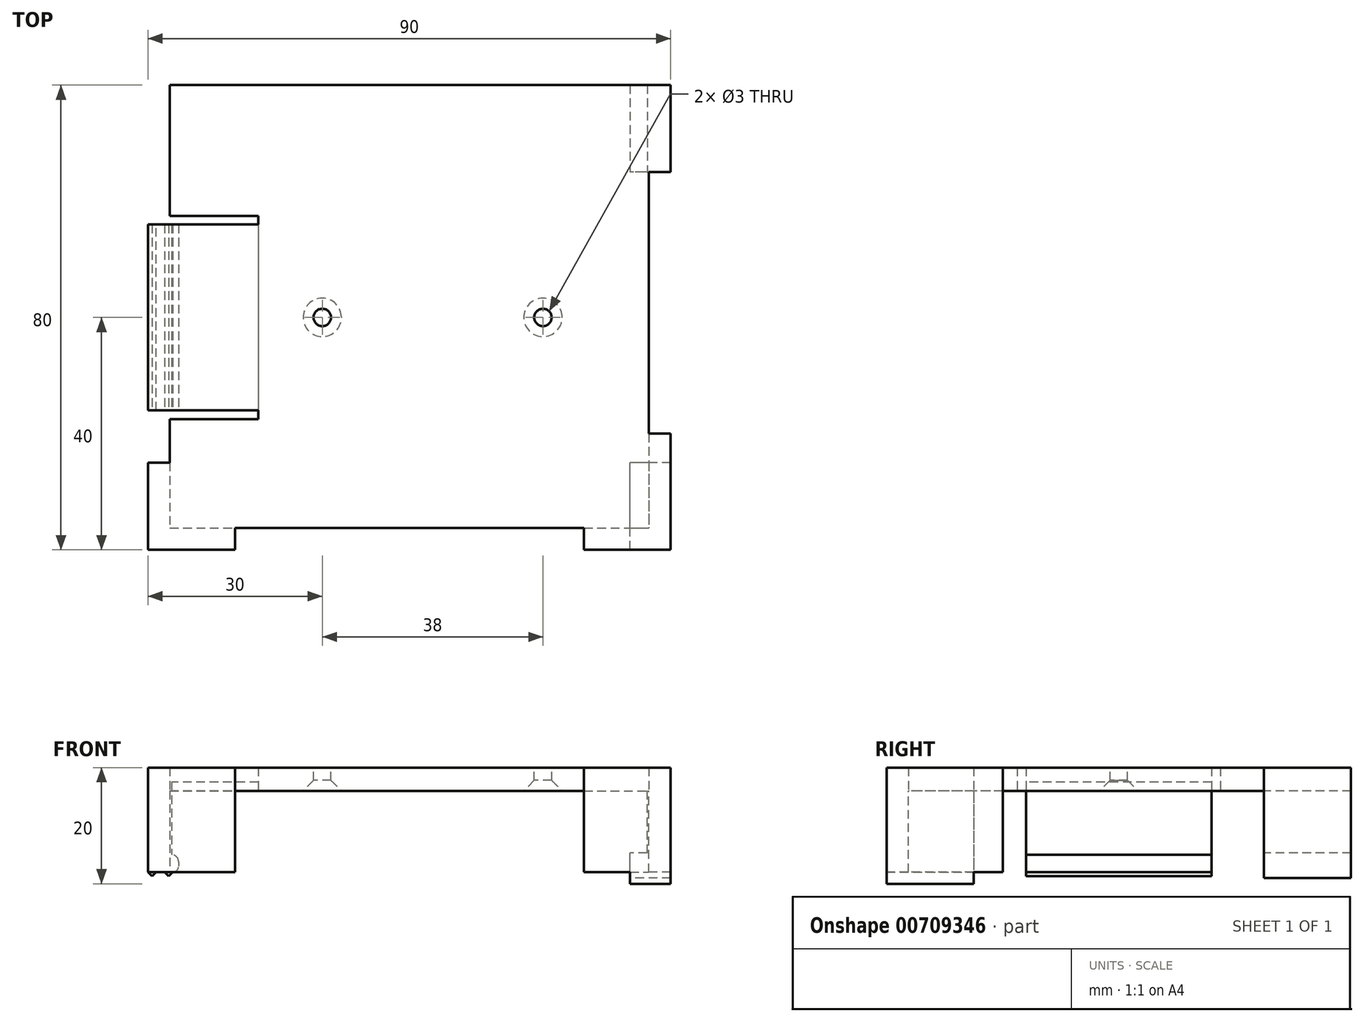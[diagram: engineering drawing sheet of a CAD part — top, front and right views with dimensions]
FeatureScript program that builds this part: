
annotation { "Feature Type Name" : "Feature", "Feature Type Description" : "" }
export const myFeature = defineFeature(function(context is Context, id is Id, definition is map)
    precondition{}
    {
        {
            var Q0;
            Q0=qCreatedBy(makeId("Top.planeOp"),FACE);
            var sketch = newSketch(context, id + "F0", { "sketchPlane" : qUnion([Q0])});
            skLineSegment(sketch, "E0.bottom", {"start": v(-45, -40) * mm, "end": v(45, -40) * mm});
            skLineSegment(sketch, "E0.top", {"start": v(-45, 40) * mm, "end": v(45, 40) * mm});
            skLineSegment(sketch, "E0.left", {"start": v(-45, -40) * mm, "end": v(-45, 40) * mm});
            skLineSegment(sketch, "E0.right", {"start": v(45, -40) * mm, "end": v(45, 40) * mm});
            skPoint(sketch, "E0.middle", {"position": v(0, 0) * mm});
            skSolve(sketch);
        }
        {
            var Q0;
            Q0 = qSketchRegion(id + "F0", true);
            extrude(context, id + "F1", {"entities" : qUnion([Q0]), "depth" : 4 * mm, "offsetDistance" : 25 * mm});
        }
        {
            var Q0;
            Q0=makeQuery(id+"F1.opExtrude","CAP_FACE",FACE,{"disambiguationData":[OSD([sQuery(id+"F0.wireOp",EDGE,"E0.bottom"),sQuery(id+"F0.wireOp",EDGE,"E0.top"),sQuery(id+"F0.wireOp",EDGE,"E0.left"),sQuery(id+"F0.wireOp",EDGE,"E0.right")])],"isStart":false});
            var sketch = newSketch(context, id + "F2", { "sketchPlane" : qUnion([Q0])});
            skCircle(sketch, "E1", {"center": v(23, 0) * mm, "radius": 1.5 * mm});
            skCircle(sketch, "E2", {"center": v(-15, 0) * mm, "radius": 1.5 * mm});
            skSolve(sketch);
        }
        {
            var Q0;
            Q0 = qSketchRegion(id + "F2", true);
            extrude(context, id + "F3", {"entities" : qUnion([Q0]), "operationType" : NewBodyOperationType.REMOVE, "endBound" : BoundingType.THROUGH_ALL, "oppositeDirection" : true, "depth" : 25 * mm, "offsetDistance" : 25 * mm});
        }
        {
            var Q0;
            Q0=makeQuery(id+"F1.opExtrude","CAP_FACE",FACE,{"disambiguationData":[OSD([sQuery(id+"F0.wireOp",EDGE,"E0.bottom"),sQuery(id+"F0.wireOp",EDGE,"E0.top"),sQuery(id+"F0.wireOp",EDGE,"E0.left"),sQuery(id+"F0.wireOp",EDGE,"E0.right")])],"isStart":true});
            var sketch = newSketch(context, id + "F4", { "sketchPlane" : qUnion([Q0])});
            skLineSegment(sketch, "E3.top", {"start": v(-41.25, 36.25) * mm, "end": v(-30, 36.25) * mm});
            skLineSegment(sketch, "E3.left", {"start": v(-41.25, -36.25) * mm, "end": v(-41.25, 36.25) * mm});
            skLineSegment(sketch, "E3.right", {"start": v(41.25, -36.25) * mm, "end": v(41.25, 36.25) * mm});
            skPoint(sketch, "E3.middle", {"position": v(0, 0) * mm});
            skLineSegment(sketch, "E4.top", {"start": v(-41.25, -40) * mm, "end": v(41.25, -40) * mm});
            skLineSegment(sketch, "E5", {"start": v(41.25, -40) * mm, "end": v(41.25, -36.25) * mm});
            skLineSegment(sketch, "E6", {"start": v(-41.25, -40) * mm, "end": v(-41.25, -36.25) * mm});
            skLineSegment(sketch, "E7.left", {"start": v(30, 36.25) * mm, "end": v(30, 40) * mm});
            skLineSegment(sketch, "E7.right", {"start": v(-30, 36.25) * mm, "end": v(-30, 40) * mm});
            skLineSegment(sketch, "E8.trimOffspring", {"start": v(30, 36.25) * mm, "end": v(41.25, 36.25) * mm});
            skSolve(sketch);
        }
        {
            var Q0;
            Q0=makeQuery(id+"F4.imprint","IMPRINT",FACE,{"disambiguationData":[TD([[makeQuery(id+"F4.imprint","IMPRINT",EDGE,{"derivedFrom":sQuery(id+"F4.wireOp",EDGE,"E3.top")}),1.0]])]});
            var Q1;
            Q1=makeQuery(id+"F4.imprint","IMPRINT",FACE,{"disambiguationData":[TD([[makeQuery(id+"F4.imprint","IMPRINT",EDGE,{"derivedFrom":sQuery(id+"F4.wireOp",EDGE,"E3.right")}),-1.0]])]});
            extrude(context, id + "F5", {"entities" : qUnion([Q0, Q1]), "operationType" : NewBodyOperationType.ADD, "depth" : 14 * mm, "offsetDistance" : 25 * mm});
        }
        {
            var Q0;
            Q0=makeQuery(id+"F5.opExtrude","CAP_FACE",FACE,{"disambiguationData":[OSD([sQuery(id+"F0.wireOp",EDGE,"E0.bottom"),sQuery(id+"F0.wireOp",EDGE,"E0.top"),sQuery(id+"F0.wireOp",EDGE,"E0.left"),sQuery(id+"F0.wireOp",EDGE,"E0.right"),sQuery(id+"F4.wireOp",EDGE,"E3.top"),sQuery(id+"F4.wireOp",EDGE,"E3.left"),sQuery(id+"F4.wireOp",EDGE,"E3.right"),sQuery(id+"F4.wireOp",EDGE,"E5"),sQuery(id+"F4.wireOp",EDGE,"E6")])],"isStart":false});
            var sketch = newSketch(context, id + "F6", { "sketchPlane" : qUnion([Q0])});
            skLineSegment(sketch, "E9.top", {"start": v(45, 25) * mm, "end": v(38, 25) * mm});
            skLineSegment(sketch, "E9.right", {"start": v(38, 40) * mm, "end": v(38, 25) * mm});
            skLineSegment(sketch, "E10", {"start": v(45, 40) * mm, "end": v(38, 40) * mm});
            skLineSegment(sketch, "E11", {"start": v(45, 40) * mm, "end": v(45, 25) * mm});
            skSolve(sketch);
        }
        {
            var Q0;
            Q0 = qSketchRegion(id + "F6", true);
            extrude(context, id + "F7", {"entities" : qUnion([Q0]), "operationType" : NewBodyOperationType.ADD, "depth" : 2 * mm, "offsetDistance" : 25 * mm});
        }
        {
            var Q0;
            {var subQ0=sQuery(id+"F4.wireOp",EDGE,"E5");var subQ1=sQuery(id+"F4.wireOp",EDGE,"E3.right");var subQ2=sQuery(id+"F0.wireOp",EDGE,"E0.right");var subQ3=sQuery(id+"F0.wireOp",EDGE,"E0.top");var subQ4=sQuery(id+"F0.wireOp",EDGE,"E0.left");var subQ6=sQuery(id+"F4.wireOp",EDGE,"E6");Q0=makeQuery(id+"F7.boolean.opBoolean","SPLIT",FACE,{"disambiguationData":[TD([makeQuery(id+"F1.opExtrude","SWEPT_FACE",FACE,{"disambiguationData":[OSD([subQ2])]})])],"derivedFrom":makeQuery(id+"F5.opExtrude","CAP_FACE",FACE,{"disambiguationData":[OSD([sQuery(id+"F0.wireOp",EDGE,"E0.bottom"),subQ3,subQ4,subQ2,sQuery(id+"F4.wireOp",EDGE,"E3.top"),sQuery(id+"F4.wireOp",EDGE,"E3.left"),subQ1,subQ0,subQ6])],"isStart":false})});}
            var sketch = newSketch(context, id + "F8", { "sketchPlane" : qUnion([Q0])});
            skLineSegment(sketch, "E12.bottom", {"start": v(45, -40) * mm, "end": v(41.25, -40) * mm});
            skLineSegment(sketch, "E12.top", {"start": v(45, 20) * mm, "end": v(41.25, 20) * mm});
            skLineSegment(sketch, "E12.left", {"start": v(45, -40) * mm, "end": v(45, 20) * mm});
            skLineSegment(sketch, "E12.right", {"start": v(41.25, -40) * mm, "end": v(41.25, 20) * mm});
            skSolve(sketch);
        }
        {
            var Q0;
            Q0 = qSketchRegion(id + "F8", true);
            extrude(context, id + "F9", {"entities" : qUnion([Q0]), "operationType" : NewBodyOperationType.REMOVE, "oppositeDirection" : true, "depth" : 2 * mm, "offsetDistance" : 25 * mm});
        }
        {
            var Q0;
            Q0=makeQuery(id+"F9.boolean.opBoolean","COPY",FACE,{"derivedFrom":makeQuery(id+"F9.opExtrude","CAP_FACE",FACE,{"disambiguationData":[OSD([sQuery(id+"F8.wireOp",EDGE,"E12.bottom"),sQuery(id+"F8.wireOp",EDGE,"E12.top"),sQuery(id+"F8.wireOp",EDGE,"E12.left"),sQuery(id+"F8.wireOp",EDGE,"E12.right")])],"isStart":false})});
            var sketch = newSketch(context, id + "F10", { "sketchPlane" : qUnion([Q0])});
            skLineSegment(sketch, "E13.bottom", {"start": v(45, -40) * mm, "end": v(41.25, -40) * mm});
            skLineSegment(sketch, "E13.top", {"start": v(45, -25) * mm, "end": v(41.25, -25) * mm});
            skLineSegment(sketch, "E13.left", {"start": v(45, -40) * mm, "end": v(45, -25) * mm});
            skLineSegment(sketch, "E14.bottom", {"start": v(41.25, -40) * mm, "end": v(38, -40) * mm});
            skLineSegment(sketch, "E14.top", {"start": v(41.25, -25) * mm, "end": v(38, -25) * mm});
            skLineSegment(sketch, "E14.left", {"start": v(41.25, -40) * mm, "end": v(41.25, -25) * mm});
            skLineSegment(sketch, "E14.right", {"start": v(38, -40) * mm, "end": v(38, -25) * mm});
            skSolve(sketch);
        }
        {
            var Q0;
            Q0 = qSketchRegion(id + "F10", true);
            extrude(context, id + "F11", {"entities" : qUnion([Q0]), "operationType" : NewBodyOperationType.ADD, "depth" : 3 * mm, "offsetDistance" : 25 * mm});
        }
        {
            var Q0;
            Q0=makeQuery(id+"F9.boolean.opBoolean","COPY",FACE,{"derivedFrom":makeQuery(id+"F9.opExtrude","CAP_FACE",FACE,{"disambiguationData":[OSD([sQuery(id+"F8.wireOp",EDGE,"E12.bottom"),sQuery(id+"F8.wireOp",EDGE,"E12.top"),sQuery(id+"F8.wireOp",EDGE,"E12.left"),sQuery(id+"F8.wireOp",EDGE,"E12.right")])],"isStart":false})});
            var sketch = newSketch(context, id + "F12", { "sketchPlane" : qUnion([Q0])});
            skLineSegment(sketch, "E15.bottom", {"start": v(45, -25) * mm, "end": v(41.25, -25) * mm});
            skLineSegment(sketch, "E15.top", {"start": v(45, 20) * mm, "end": v(41.25, 20) * mm});
            skLineSegment(sketch, "E15.left", {"start": v(45, -25) * mm, "end": v(45, 20) * mm});
            skLineSegment(sketch, "E15.right", {"start": v(41.25, -25) * mm, "end": v(41.25, 20) * mm});
            skSolve(sketch);
        }
        {
            var Q0;
            Q0 = qSketchRegion(id + "F12", true);
            extrude(context, id + "F13", {"entities" : qUnion([Q0]), "operationType" : NewBodyOperationType.REMOVE, "endBound" : BoundingType.THROUGH_ALL, "oppositeDirection" : true, "depth" : 25 * mm, "offsetDistance" : 25 * mm});
        }
        {
            var Q0;
            {var subQ0=sQuery(id+"F0.wireOp",EDGE,"E0.right");var subQ1=sQuery(id+"F0.wireOp",EDGE,"E0.top");var subQ3=sQuery(id+"F4.wireOp",EDGE,"E5");var subQ5=sQuery(id+"F0.wireOp",EDGE,"E0.left");var subQ6=sQuery(id+"F4.wireOp",EDGE,"E6");var subQ9=sQuery(id+"F0.wireOp",EDGE,"E0.bottom");var subQ10=sQuery(id+"F4.wireOp",EDGE,"E3.top");var subQ11=sQuery(id+"F4.wireOp",EDGE,"E3.left");Q0=makeQuery(id+"F7.boolean.opBoolean","SPLIT",FACE,{"disambiguationData":[TD([makeQuery(id+"F1.opExtrude","SWEPT_FACE",FACE,{"disambiguationData":[OSD([subQ9])]})])],"derivedFrom":makeQuery(id+"F5.opExtrude","CAP_FACE",FACE,{"disambiguationData":[OSD([subQ9,subQ1,subQ5,subQ0,subQ10,subQ11,sQuery(id+"F4.wireOp",EDGE,"E3.right"),subQ3,subQ6])],"isStart":false})});}
            var sketch = newSketch(context, id + "F14", { "sketchPlane" : qUnion([Q0])});
            skLineSegment(sketch, "E16.bottom", {"start": v(-45, 16) * mm, "end": v(-26, 16) * mm});
            skLineSegment(sketch, "E16.top", {"start": v(-45, 17.5) * mm, "end": v(-26, 17.5) * mm});
            skLineSegment(sketch, "E16.left", {"start": v(-45, 16) * mm, "end": v(-45, 17.5) * mm});
            skLineSegment(sketch, "E16.right", {"start": v(-26, 16) * mm, "end": v(-26, 17.5) * mm});
            skLineSegment(sketch, "E17.bottom", {"start": v(-45, -16) * mm, "end": v(-26, -16) * mm});
            skLineSegment(sketch, "E17.top", {"start": v(-45, -17.5) * mm, "end": v(-26, -17.5) * mm});
            skLineSegment(sketch, "E17.left", {"start": v(-45, -16) * mm, "end": v(-45, -17.5) * mm});
            skLineSegment(sketch, "E17.right", {"start": v(-26, -16) * mm, "end": v(-26, -17.5) * mm});
            skSolve(sketch);
        }
        {
            var Q0;
            Q0 = qSketchRegion(id + "F14", true);
            extrude(context, id + "F15", {"entities" : qUnion([Q0]), "operationType" : NewBodyOperationType.REMOVE, "oppositeDirection" : true, "depth" : 25 * mm, "offsetDistance" : 25 * mm});
        }
        {
            var Q0;
            {var subQ0=sQuery(id+"F4.wireOp",EDGE,"E6");var subQ1=sQuery(id+"F4.wireOp",EDGE,"E3.left");var subQ3=sQuery(id+"F0.wireOp",EDGE,"E0.left");var subQ6=sQuery(id+"F0.wireOp",EDGE,"E0.top");var subQ7=makeQuery(id+"F1.opExtrude","SWEPT_FACE",FACE,{"disambiguationData":[OSD([subQ6])]});var subQ11=sQuery(id+"F0.wireOp",EDGE,"E0.right");var subQ12=sQuery(id+"F4.wireOp",EDGE,"E5");var subQ16=sQuery(id+"F0.wireOp",EDGE,"E0.bottom");var subQ17=sQuery(id+"F4.wireOp",EDGE,"E3.top");Q0=makeQuery(id+"F15.boolean.opBoolean","SPLIT",FACE,{"disambiguationData":[TD([subQ7])],"derivedFrom":makeQuery(id+"F7.boolean.opBoolean","SPLIT",FACE,{"disambiguationData":[TD([makeQuery(id+"F1.opExtrude","SWEPT_FACE",FACE,{"disambiguationData":[OSD([subQ16])]})])],"derivedFrom":makeQuery(id+"F5.opExtrude","CAP_FACE",FACE,{"disambiguationData":[OSD([subQ16,subQ6,subQ3,subQ11,subQ17,subQ1,sQuery(id+"F4.wireOp",EDGE,"E3.right"),subQ12,subQ0])],"isStart":false})})});}
            var sketch = newSketch(context, id + "F16", { "sketchPlane" : qUnion([Q0])});
            skLineSegment(sketch, "E18.bottom", {"start": v(-41.25, -40) * mm, "end": v(-45, -40) * mm});
            skLineSegment(sketch, "E18.top", {"start": v(-41.25, -17.5) * mm, "end": v(-45, -17.5) * mm});
            skLineSegment(sketch, "E18.left", {"start": v(-41.25, -40) * mm, "end": v(-41.25, -17.5) * mm});
            skLineSegment(sketch, "E18.right", {"start": v(-45, -40) * mm, "end": v(-45, -17.5) * mm});
            skSolve(sketch);
        }
        {
            var Q0;
            Q0 = qSketchRegion(id + "F16", true);
            var Q1;
            Q1=makeQuery(id+"F1.opExtrude","CAP_FACE",FACE,{"disambiguationData":[OSD([sQuery(id+"F0.wireOp",EDGE,"E0.bottom"),sQuery(id+"F0.wireOp",EDGE,"E0.top"),sQuery(id+"F0.wireOp",EDGE,"E0.left"),sQuery(id+"F0.wireOp",EDGE,"E0.right")])],"isStart":true});
            extrude(context, id + "F17", {"entities" : qUnion([Q0]), "operationType" : NewBodyOperationType.REMOVE, "oppositeDirection" : true, "depth" : 25 * mm, "endBoundEntityFace" : qUnion([Q1]), "offsetDistance" : 25 * mm});
        }
        {
            var Q0;
            {var subQ4=sQuery(id+"F4.wireOp",EDGE,"E6");var subQ5=sQuery(id+"F4.wireOp",EDGE,"E3.left");Q0=makeQuery(id+"F15.boolean.opBoolean","SPLIT",FACE,{"disambiguationData":[TD([makeQuery(id+"F15.opExtrude","SWEPT_FACE",FACE,{"disambiguationData":[OSD([sQuery(id+"F14.wireOp",EDGE,"E16.bottom")])]})])],"derivedFrom":makeQuery(id+"F5.opExtrude","SWEPT_FACE",FACE,{"disambiguationData":[OSD([subQ5,subQ4])]})});}
            var sketch = newSketch(context, id + "F18", { "sketchPlane" : qUnion([Q0])});
            skLineSegment(sketch, "E19.bottom", {"start": v(16, -14) * mm, "end": v(-16, -14) * mm});
            skLineSegment(sketch, "E19.top", {"start": v(16, -12) * mm, "end": v(-16, -12) * mm});
            skLineSegment(sketch, "E19.left", {"start": v(16, -14) * mm, "end": v(16, -12) * mm});
            skLineSegment(sketch, "E19.right", {"start": v(-16, -14) * mm, "end": v(-16, -12) * mm});
            skSolve(sketch);
        }
        {
            var Q0;
            Q0=makeQuery(id+"F18.imprint","IMPRINT",FACE,{"disambiguationData":[TD([[makeQuery(id+"F18.imprint","IMPRINT",EDGE,{"derivedFrom":sQuery(id+"F18.wireOp",EDGE,"E19.bottom")}),-1.0]])]});
            extrude(context, id + "F19", {"entities" : qUnion([Q0]), "operationType" : NewBodyOperationType.ADD, "depth" : 1.5 * mm, "offsetDistance" : 25 * mm});
        }
        {
            var Q0;
            Q0=makeQuery(id+"F19.opExtrude","CAP_EDGE",EDGE,{"disambiguationData":[OSD([sQuery(id+"F18.wireOp",EDGE,"E19.bottom")])],"isStart":false});
            fillet(context, id + "F20", {"entities" : qUnion([Q0]), "radius" : 1 * mm, "tangentPropagation" : true, "allowEdgeOverflow" : false});
        }
        {
            var Q0;
            {var subQ0=sQuery(id+"F4.wireOp",EDGE,"E6");var subQ1=sQuery(id+"F4.wireOp",EDGE,"E3.left");var subQ3=sQuery(id+"F0.wireOp",EDGE,"E0.left");var subQ6=sQuery(id+"F0.wireOp",EDGE,"E0.right");var subQ7=sQuery(id+"F0.wireOp",EDGE,"E0.top");var subQ9=sQuery(id+"F4.wireOp",EDGE,"E5");var subQ13=sQuery(id+"F0.wireOp",EDGE,"E0.bottom");var subQ14=sQuery(id+"F4.wireOp",EDGE,"E3.top");Q0=makeQuery(id+"F19.boolean.opBoolean","MERGE",FACE,{"derivedFrom":[makeQuery(id+"F15.boolean.opBoolean","SPLIT",FACE,{"disambiguationData":[TD([makeQuery(id+"F15.opExtrude","SWEPT_FACE",FACE,{"disambiguationData":[OSD([sQuery(id+"F14.wireOp",EDGE,"E16.bottom")])]})])],"derivedFrom":makeQuery(id+"F7.boolean.opBoolean","SPLIT",FACE,{"disambiguationData":[TD([makeQuery(id+"F1.opExtrude","SWEPT_FACE",FACE,{"disambiguationData":[OSD([subQ13])]})])],"derivedFrom":makeQuery(id+"F5.opExtrude","CAP_FACE",FACE,{"disambiguationData":[OSD([subQ13,subQ7,subQ3,subQ6,subQ14,subQ1,sQuery(id+"F4.wireOp",EDGE,"E3.right"),subQ9,subQ0])],"isStart":false})})}),makeQuery(id+"F19.opExtrude","SWEPT_FACE",FACE,{"disambiguationData":[OSD([sQuery(id+"F18.wireOp",EDGE,"E19.bottom")])]})]});}
            var sketch = newSketch(context, id + "F21", { "sketchPlane" : qUnion([Q0])});
            skLineSegment(sketch, "E20.bottom", {"start": v(-40.75, -16) * mm, "end": v(-42.17, -16) * mm});
            skLineSegment(sketch, "E20.top", {"start": v(-40.75, 16) * mm, "end": v(-42.17, 16) * mm});
            skLineSegment(sketch, "E20.left", {"start": v(-40.75, -16) * mm, "end": v(-40.75, 16) * mm});
            skLineSegment(sketch, "E20.right", {"start": v(-42.17, -16) * mm, "end": v(-42.17, 16) * mm});
            skLineSegment(sketch, "E21.bottom", {"start": v(-45, 16) * mm, "end": v(-43.58, 16) * mm});
            skLineSegment(sketch, "E21.top", {"start": v(-45, -16) * mm, "end": v(-43.58, -16) * mm});
            skLineSegment(sketch, "E21.left", {"start": v(-45, 16) * mm, "end": v(-45, -16) * mm});
            skLineSegment(sketch, "E21.right", {"start": v(-43.58, 16) * mm, "end": v(-43.58, -16) * mm});
            skSolve(sketch);
        }
        {
            var Q0;
            Q0 = qSketchRegion(id + "F21", true);
            extrude(context, id + "F22", {"entities" : qUnion([Q0]), "operationType" : NewBodyOperationType.ADD, "depth" : (1.42 / 2) * mm, "offsetDistance" : 25 * mm});
        }
        {
            var Q0;
            Q0=makeQuery(id+"F22.opExtrude","CAP_EDGE",EDGE,{"disambiguationData":[OSD([sQuery(id+"F21.wireOp",EDGE,"E20.left")])],"isStart":false});
            var Q1;
            Q1=makeQuery(id+"F22.opExtrude","CAP_EDGE",EDGE,{"disambiguationData":[OSD([sQuery(id+"F21.wireOp",EDGE,"E20.right")])],"isStart":false});
            var Q2;
            Q2=makeQuery(id+"F22.opExtrude","CAP_EDGE",EDGE,{"disambiguationData":[OSD([sQuery(id+"F21.wireOp",EDGE,"o1l8Pqun-URdb-0TMV-Lpvj-JEDRhUXDJmeT.right")])],"isStart":false});
            var Q3;
            Q3=makeQuery(id+"F22.opExtrude","CAP_EDGE",EDGE,{"disambiguationData":[OSD([sQuery(id+"F21.wireOp",EDGE,"o1l8Pqun-URdb-0TMV-Lpvj-JEDRhUXDJmeT.left")])],"isStart":false});
            var Q4;
            Q4=makeQuery(id+"F22.opExtrude","CAP_EDGE",EDGE,{"disambiguationData":[OSD([sQuery(id+"F21.wireOp",EDGE,"E21.right")])],"isStart":false});
            var Q5;
            Q5=makeQuery(id+"F22.opExtrude","CAP_EDGE",EDGE,{"disambiguationData":[OSD([sQuery(id+"F21.wireOp",EDGE,"E21.left")])],"isStart":false});
            chamfer(context, id + "F23", {"entities" : qUnion([Q0, Q1, Q2, Q3, Q4, Q5]), "width" : (1.42 / 2) * mm, "tangentPropagation" : true});
        }
        {
            var Q0;
            Q0=makeQuery(id+"F3.boolean.opBoolean","INTERSECT",EDGE,{"derivedFrom":[makeQuery(id+"F1.opExtrude","CAP_FACE",FACE,{"disambiguationData":[OSD([sQuery(id+"F0.wireOp",EDGE,"E0.bottom"),sQuery(id+"F0.wireOp",EDGE,"E0.top"),sQuery(id+"F0.wireOp",EDGE,"E0.left"),sQuery(id+"F0.wireOp",EDGE,"E0.right")])],"isStart":true}),makeQuery(id+"F3.opExtrude","SWEPT_FACE",FACE,{"disambiguationData":[OSD([sQuery(id+"F2.wireOp",EDGE,"E2")])]})]});
            var Q1;
            Q1=makeQuery(id+"F3.boolean.opBoolean","INTERSECT",EDGE,{"derivedFrom":[makeQuery(id+"F1.opExtrude","CAP_FACE",FACE,{"disambiguationData":[OSD([sQuery(id+"F0.wireOp",EDGE,"E0.bottom"),sQuery(id+"F0.wireOp",EDGE,"E0.top"),sQuery(id+"F0.wireOp",EDGE,"E0.left"),sQuery(id+"F0.wireOp",EDGE,"E0.right")])],"isStart":true}),makeQuery(id+"F3.opExtrude","SWEPT_FACE",FACE,{"disambiguationData":[OSD([sQuery(id+"F2.wireOp",EDGE,"E1")])]})]});
            chamfer(context, id + "F24", {"entities" : qUnion([Q0, Q1]), "width" : 1.8 * mm, "tangentPropagation" : true});
        }
        {
            var Q0;
            {var subQ0=sQuery(id+"F4.wireOp",EDGE,"E6");var subQ1=sQuery(id+"F4.wireOp",EDGE,"E3.left");var subQ3=sQuery(id+"F0.wireOp",EDGE,"E0.left");var subQ5=sQuery(id+"F4.wireOp",EDGE,"E3.top");var subQ7=sQuery(id+"F0.wireOp",EDGE,"E0.bottom");var subQ8=makeQuery(id+"F1.opExtrude","SWEPT_FACE",FACE,{"disambiguationData":[OSD([subQ7])]});var subQ16=sQuery(id+"F0.wireOp",EDGE,"E0.right");var subQ17=sQuery(id+"F0.wireOp",EDGE,"E0.top");var subQ19=sQuery(id+"F4.wireOp",EDGE,"E5");Q0=makeQuery(id+"F15.boolean.opBoolean","SPLIT",FACE,{"disambiguationData":[TD([subQ8])],"derivedFrom":makeQuery(id+"F7.boolean.opBoolean","SPLIT",FACE,{"disambiguationData":[TD([subQ8])],"derivedFrom":makeQuery(id+"F5.opExtrude","CAP_FACE",FACE,{"disambiguationData":[OSD([subQ7,subQ17,subQ3,subQ16,subQ5,subQ1,sQuery(id+"F4.wireOp",EDGE,"E3.right"),subQ19,subQ0])],"isStart":false})})});}
            var sketch = newSketch(context, id + "F25", { "sketchPlane" : qUnion([Q0])});
            skLineSegment(sketch, "E22.bottom", {"start": v(-45, 17.5) * mm, "end": v(-41.25, 17.5) * mm});
            skLineSegment(sketch, "E22.top", {"start": v(-45, 25) * mm, "end": v(-41.25, 25) * mm});
            skLineSegment(sketch, "E22.left", {"start": v(-45, 17.5) * mm, "end": v(-45, 25) * mm});
            skLineSegment(sketch, "E22.right", {"start": v(-41.25, 17.5) * mm, "end": v(-41.25, 25) * mm});
            skLineSegment(sketch, "E23.right", {"start": v(-30, 36.25) * mm, "end": v(-30, 40) * mm});
            skLineSegment(sketch, "E24.bottom", {"start": v(-30, 36.25) * mm, "end": v(30.06, 36.25) * mm});
            skLineSegment(sketch, "E24.top", {"start": v(-30, 40) * mm, "end": v(30.06, 40) * mm});
            skLineSegment(sketch, "E24.right", {"start": v(30.06, 36.25) * mm, "end": v(30.06, 40) * mm});
            skSolve(sketch);
        }
        {
            var Q0;
            Q0 = qSketchRegion(id + "F25", true);
            extrude(context, id + "F26", {"entities" : qUnion([Q0]), "operationType" : NewBodyOperationType.REMOVE, "oppositeDirection" : true, "depth" : 25 * mm, "offsetDistance" : 25 * mm});
        }
        {
            var Q0;
            Q0=makeQuery(id+"F1.opExtrude","CAP_FACE",FACE,{"disambiguationData":[OSD([sQuery(id+"F0.wireOp",EDGE,"E0.bottom"),sQuery(id+"F0.wireOp",EDGE,"E0.top"),sQuery(id+"F0.wireOp",EDGE,"E0.left"),sQuery(id+"F0.wireOp",EDGE,"E0.right")])],"isStart":true});
            var sketch = newSketch(context, id + "F27", { "sketchPlane" : qUnion([Q0])});
            skLineSegment(sketch, "E25.bottom", {"start": v(-26, -16) * mm, "end": v(-41.25, -16) * mm});
            skLineSegment(sketch, "E25.top", {"start": v(-26, 16) * mm, "end": v(-41.25, 16) * mm});
            skLineSegment(sketch, "E25.left", {"start": v(-26, -16) * mm, "end": v(-26, 16) * mm});
            skLineSegment(sketch, "E25.right", {"start": v(-41.25, -16) * mm, "end": v(-41.25, 16) * mm});
            skSolve(sketch);
        }
        {
            var Q0;
            Q0 = qSketchRegion(id + "F27", true);
            extrude(context, id + "F28", {"entities" : qUnion([Q0]), "operationType" : NewBodyOperationType.REMOVE, "oppositeDirection" : true, "depth" : 1.5 * mm, "offsetDistance" : 25 * mm});
        }
        {
            var Q0;
            {var subQ3=sQuery(id+"F4.wireOp",EDGE,"E6");var subQ4=sQuery(id+"F4.wireOp",EDGE,"E3.left");Q0=makeQuery(id+"F28.boolean.opBoolean","MERGE",FACE,{"derivedFrom":[makeQuery(id+"F15.boolean.opBoolean","SPLIT",FACE,{"disambiguationData":[TD([makeQuery(id+"F15.opExtrude","SWEPT_FACE",FACE,{"disambiguationData":[OSD([sQuery(id+"F14.wireOp",EDGE,"E16.bottom")])]})])],"derivedFrom":makeQuery(id+"F5.opExtrude","SWEPT_FACE",FACE,{"disambiguationData":[OSD([subQ4,subQ3])]})}),makeQuery(id+"F28.opExtrude","SWEPT_FACE",FACE,{"disambiguationData":[OSD([sQuery(id+"F27.wireOp",EDGE,"E25.right")])]})]});}
            var sketch = newSketch(context, id + "F29", { "sketchPlane" : qUnion([Q0])});
            skLineSegment(sketch, "E26.bottom", {"start": v(-16, 1.5) * mm, "end": v(16, 1.5) * mm});
            skLineSegment(sketch, "E26.top", {"start": v(-16, -12) * mm, "end": v(16, -12) * mm});
            skLineSegment(sketch, "E26.left", {"start": v(-16, 1.5) * mm, "end": v(-16, -12) * mm});
            skLineSegment(sketch, "E26.right", {"start": v(16, 1.5) * mm, "end": v(16, -12) * mm});
            skSolve(sketch);
        }
        {
            var Q0;
            Q0 = qSketchRegion(id + "F29", true);
            extrude(context, id + "F30", {"entities" : qUnion([Q0]), "operationType" : NewBodyOperationType.ADD, "depth" : 0.3 * mm, "offsetDistance" : 25 * mm});
        }
        {
            var Q0;
            Q0=makeQuery(id+"F11.opExtrude","CAP_FACE",FACE,{"disambiguationData":[OSD([sQuery(id+"F10.wireOp",EDGE,"E13.bottom"),sQuery(id+"F10.wireOp",EDGE,"E13.top"),sQuery(id+"F10.wireOp",EDGE,"E13.left"),sQuery(id+"F10.wireOp",EDGE,"E14.bottom"),sQuery(id+"F10.wireOp",EDGE,"E14.top"),sQuery(id+"F10.wireOp",EDGE,"E14.right")])],"isStart":true});
            var sketch = newSketch(context, id + "F31", { "sketchPlane" : qUnion([Q0])});
            skLineSegment(sketch, "E27.bottom", {"start": v(41.25, 25) * mm, "end": v(38, 25) * mm});
            skLineSegment(sketch, "E27.top", {"start": v(41.25, 40) * mm, "end": v(38, 40) * mm});
            skLineSegment(sketch, "E27.left", {"start": v(41.25, 25) * mm, "end": v(41.25, 40) * mm});
            skLineSegment(sketch, "E27.right", {"start": v(38, 25) * mm, "end": v(38, 40) * mm});
            skSolve(sketch);
        }
        {
            var Q0;
            Q0 = qSketchRegion(id + "F31", true);
            extrude(context, id + "F32", {"entities" : qUnion([Q0]), "operationType" : NewBodyOperationType.ADD, "depth" : 1.3 * mm, "offsetDistance" : 25 * mm});
        }
        {
            var Q0;
            {var subQ1=sQuery(id+"F0.wireOp",EDGE,"E0.top");var subQ3=sQuery(id+"F4.wireOp",EDGE,"E5");Q0=makeQuery(id+"F13.boolean.opBoolean","SPLIT",FACE,{"disambiguationData":[TD([makeQuery(id+"F1.opExtrude","SWEPT_FACE",FACE,{"disambiguationData":[OSD([subQ1])]})])],"derivedFrom":makeQuery(id+"F5.opExtrude","SWEPT_FACE",FACE,{"disambiguationData":[OSD([sQuery(id+"F4.wireOp",EDGE,"E3.right"),subQ3])]})});}
            var sketch = newSketch(context, id + "F33", { "sketchPlane" : qUnion([Q0])});
            skLineSegment(sketch, "E28.bottom", {"start": v(-40, 0) * mm, "end": v(-25, 0) * mm});
            skLineSegment(sketch, "E28.top", {"start": v(-40, -10.7) * mm, "end": v(-25, -10.7) * mm});
            skLineSegment(sketch, "E28.left", {"start": v(-40, 0) * mm, "end": v(-40, -10.7) * mm});
            skLineSegment(sketch, "E28.right", {"start": v(-25, 0) * mm, "end": v(-25, -10.7) * mm});
            skSolve(sketch);
        }
        {
            var Q0;
            Q0 = qSketchRegion(id + "F33", true);
            extrude(context, id + "F34", {"entities" : qUnion([Q0]), "operationType" : NewBodyOperationType.ADD, "depth" : 0.3 * mm, "offsetDistance" : 25 * mm});
        }
        {
            var Q0;
            Q0=makeQuery(id+"F19.opExtrude","SWEPT_FACE",FACE,{"disambiguationData":[OSD([sQuery(id+"F18.wireOp",EDGE,"E19.top")])]});
            var sketch = newSketch(context, id + "F35", { "sketchPlane" : qUnion([Q0])});
            skLineSegment(sketch, "E29.bottom", {"start": v(-40.95, 16) * mm, "end": v(-39.75, 16) * mm});
            skLineSegment(sketch, "E29.top", {"start": v(-40.95, -16) * mm, "end": v(-39.75, -16) * mm});
            skLineSegment(sketch, "E29.left", {"start": v(-40.95, 16) * mm, "end": v(-40.95, -16) * mm});
            skLineSegment(sketch, "E29.right", {"start": v(-39.75, 16) * mm, "end": v(-39.75, -16) * mm});
            skSolve(sketch);
        }
        {
            var Q0;
            Q0 = qSketchRegion(id + "F35", true);
            extrude(context, id + "F36", {"entities" : qUnion([Q0]), "operationType" : NewBodyOperationType.ADD, "depth" : 1 * mm, "offsetDistance" : 25 * mm});
        }
        {
            var Q0;
            Q0=makeQuery(id+"F36.opExtrude","CAP_EDGE",EDGE,{"disambiguationData":[OSD([sQuery(id+"F35.wireOp",EDGE,"E29.right")])],"isStart":false});
            fillet(context, id + "F37", {"entities" : qUnion([Q0]), "radius" : 1.2 * mm, "tangentPropagation" : true, "allowEdgeOverflow" : false});
        }
    });
